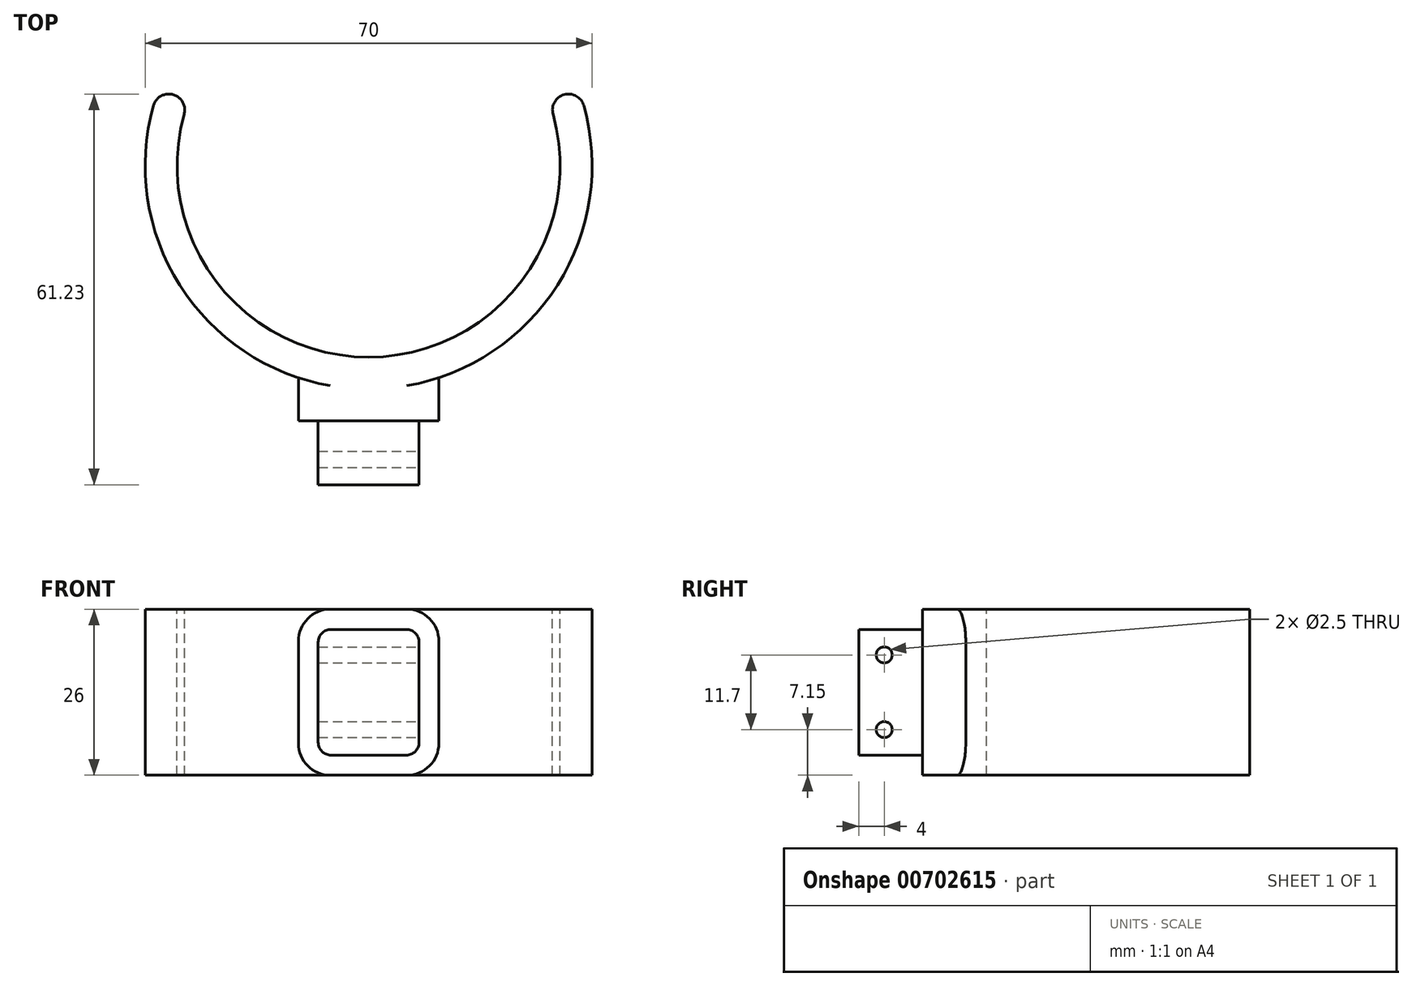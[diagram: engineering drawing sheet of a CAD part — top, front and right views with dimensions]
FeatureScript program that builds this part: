
annotation { "Feature Type Name" : "Feature", "Feature Type Description" : "" }
export const myFeature = defineFeature(function(context is Context, id is Id, definition is map)
    precondition{}
    {
        {
            var Q0;
            Q0=qCreatedBy(makeId("Right.planeOp"),FACE);
            var sketch = newSketch(context, id + "F0", { "sketchPlane" : qUnion([Q0])});
            skLineSegment(sketch, "E0.bottom", {"start": v(0, -13) * mm, "end": v(5, -13) * mm});
            skLineSegment(sketch, "E0.top", {"start": v(0, 13) * mm, "end": v(5, 13) * mm});
            skLineSegment(sketch, "E0.left", {"start": v(0, -13) * mm, "end": v(0, 13) * mm});
            skLineSegment(sketch, "E0.right", {"start": v(5, -13) * mm, "end": v(5, 13) * mm});
            skLineSegment(sketch, "E1", {"start": v(35, 60.61) * mm, "end": v(35, -54.9) * mm, "construction": true});
            skSolve(sketch);
        }
        {
            var Q0;
            Q0=qSketchRegion(id+"F0",true);
            var Q1;
            Q1=sQuery(id+"F0.wireOp",EDGE,"E1");
            revolve(context, id + "F1", {"entities" : qUnion([Q0]), "axis" : qUnion([Q1]), "revolveType" : RevolveType.SYMMETRIC, "angle" : 220 * degree});
        }
        {
            var Q0;
            Q0=qCreatedBy(makeId("Front.planeOp"),FACE);
            var sketch = newSketch(context, id + "F2", { "sketchPlane" : qUnion([Q0])});
            skLineSegment(sketch, "E2.bottom", {"start": v(11, 13) * mm, "end": v(-11, 13) * mm});
            skLineSegment(sketch, "E2.top", {"start": v(11, -13) * mm, "end": v(-11, -13) * mm});
            skLineSegment(sketch, "E2.left", {"start": v(11, 13) * mm, "end": v(11, -13) * mm});
            skLineSegment(sketch, "E2.right", {"start": v(-11, 13) * mm, "end": v(-11, -13) * mm});
            skSolve(sketch);
        }
        {
            var Q0;
            Q0=qSketchRegion(id+"F2",true);
            extrude(context, id + "F3", {"entities" : qUnion([Q0]), "operationType" : NewBodyOperationType.ADD, "depth" : 5 * mm, "hasSecondDirection" : true, "secondDirectionBound" : SecondDirectionBoundingType.UP_TO_NEXT, "secondDirectionOppositeDirection" : true, "secondDirectionDepth" : 25 * mm});
        }
        {
            var Q0;
            Q0=makeQuery(id+"F1.opRevolve","CAP_EDGE",EDGE,{"disambiguationData":[OSD([sQuery(id+"F0.wireOp",EDGE,"E0.left")])],"isStart":true});
            var Q1;
            Q1=makeQuery(id+"F1.opRevolve","CAP_EDGE",EDGE,{"disambiguationData":[OSD([sQuery(id+"F0.wireOp",EDGE,"E0.right")])],"isStart":true});
            var Q2;
            Q2=makeQuery(id+"F1.opRevolve","CAP_EDGE",EDGE,{"disambiguationData":[OSD([sQuery(id+"F0.wireOp",EDGE,"E0.right")])],"isStart":false});
            var Q3;
            Q3=makeQuery(id+"F1.opRevolve","CAP_EDGE",EDGE,{"disambiguationData":[OSD([sQuery(id+"F0.wireOp",EDGE,"E0.left")])],"isStart":false});
            fillet(context, id + "F4", {"entities" : qUnion([Q0, Q1, Q2, Q3]), "radius" : 2.5 * mm, "tangentPropagation" : true, "allowEdgeOverflow" : false});
        }
        {
            var Q0;
            Q0=makeQuery(id+"F3.opExtrude","CAP_FACE",FACE,{"disambiguationData":[OSD([sQuery(id+"F2.wireOp",EDGE,"E2.bottom"),sQuery(id+"F2.wireOp",EDGE,"E2.top"),sQuery(id+"F2.wireOp",EDGE,"E2.left"),sQuery(id+"F2.wireOp",EDGE,"E2.right")])],"isStart":false});
            var sketch = newSketch(context, id + "F5", { "sketchPlane" : qUnion([Q0])});
            skLineSegment(sketch, "E3.bottom", {"start": v(-7.9, 9.85) * mm, "end": v(7.9, 9.85) * mm});
            skLineSegment(sketch, "E3.top", {"start": v(-7.9, -9.85) * mm, "end": v(7.9, -9.85) * mm});
            skLineSegment(sketch, "E3.left", {"start": v(-7.9, 9.85) * mm, "end": v(-7.9, -9.85) * mm});
            skLineSegment(sketch, "E3.right", {"start": v(7.9, 9.85) * mm, "end": v(7.9, -9.85) * mm});
            skSolve(sketch);
        }
        {
            var Q0;
            Q0=qSketchRegion(id+"F5",true);
            extrude(context, id + "F6", {"entities" : qUnion([Q0]), "operationType" : NewBodyOperationType.ADD, "depth" : 10 * mm});
        }
        {
            var Q0;
            Q0=makeQuery(id+"F6.opExtrude","SWEPT_FACE",FACE,{"disambiguationData":[OSD([sQuery(id+"F5.wireOp",EDGE,"E3.right")])]});
            var sketch = newSketch(context, id + "F7", { "sketchPlane" : qUnion([Q0])});
            skCircle(sketch, "E4", {"center": v(-11, 5.85) * mm, "radius": 1.25 * mm});
            skCircle(sketch, "E5", {"center": v(-11, -5.85) * mm, "radius": 1.25 * mm});
            skSolve(sketch);
        }
        {
            var Q0;
            Q0=qSketchRegion(id+"F7",true);
            extrude(context, id + "F8", {"entities" : qUnion([Q0]), "operationType" : NewBodyOperationType.REMOVE, "endBound" : BoundingType.THROUGH_ALL, "oppositeDirection" : true, "depth" : 25 * mm});
        }
        {
            var Q0;
            Q0=makeQuery(id+"F6.opExtrude","SWEPT_EDGE",EDGE,{"disambiguationData":[OSD([sQuery(id+"F5.wireOp",EDGE,"E3.bottom"),sQuery(id+"F5.wireOp",EDGE,"E3.right")])]});
            var Q1;
            Q1=makeQuery(id+"F6.opExtrude","SWEPT_EDGE",EDGE,{"disambiguationData":[OSD([sQuery(id+"F5.wireOp",EDGE,"E3.top"),sQuery(id+"F5.wireOp",EDGE,"E3.right")])]});
            var Q2;
            Q2=makeQuery(id+"F6.opExtrude","SWEPT_EDGE",EDGE,{"disambiguationData":[OSD([sQuery(id+"F5.wireOp",EDGE,"E3.top"),sQuery(id+"F5.wireOp",EDGE,"E3.left")])]});
            var Q3;
            Q3=makeQuery(id+"F6.opExtrude","SWEPT_EDGE",EDGE,{"disambiguationData":[OSD([sQuery(id+"F5.wireOp",EDGE,"E3.bottom"),sQuery(id+"F5.wireOp",EDGE,"E3.left")])]});
            fillet(context, id + "F9", {"entities" : qUnion([Q0, Q1, Q2, Q3]), "radius" : 2 * mm, "tangentPropagation" : true, "allowEdgeOverflow" : false});
        }
        {
            var Q0;
            Q0=makeQuery(id+"F3.opExtrude","SWEPT_EDGE",EDGE,{"disambiguationData":[OSD([sQuery(id+"F2.wireOp",EDGE,"E2.bottom"),sQuery(id+"F2.wireOp",EDGE,"E2.right")])]});
            var Q1;
            Q1=makeQuery(id+"F3.opExtrude","SWEPT_EDGE",EDGE,{"disambiguationData":[OSD([sQuery(id+"F2.wireOp",EDGE,"E2.top"),sQuery(id+"F2.wireOp",EDGE,"E2.right")])]});
            var Q2;
            Q2=makeQuery(id+"F3.opExtrude","SWEPT_EDGE",EDGE,{"disambiguationData":[OSD([sQuery(id+"F2.wireOp",EDGE,"E2.top"),sQuery(id+"F2.wireOp",EDGE,"E2.left")])]});
            var Q3;
            Q3=makeQuery(id+"F3.opExtrude","SWEPT_EDGE",EDGE,{"disambiguationData":[OSD([sQuery(id+"F2.wireOp",EDGE,"E2.bottom"),sQuery(id+"F2.wireOp",EDGE,"E2.left")])]});
            fillet(context, id + "F10", {"entities" : qUnion([Q0, Q1, Q2, Q3]), "radius" : 5 * mm, "tangentPropagation" : true, "allowEdgeOverflow" : false});
        }
    });
